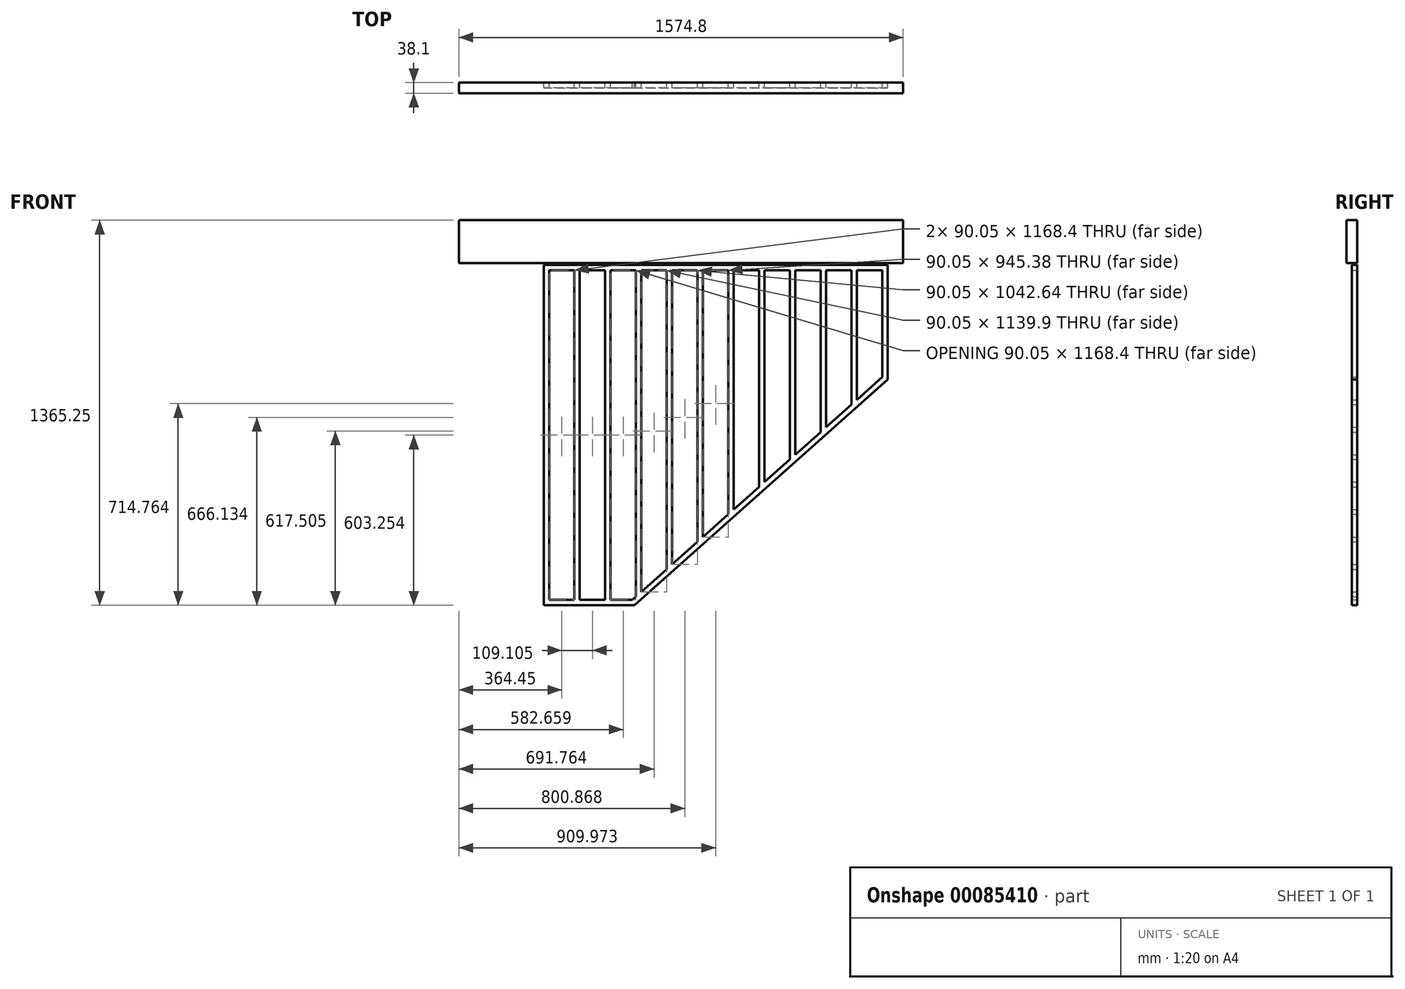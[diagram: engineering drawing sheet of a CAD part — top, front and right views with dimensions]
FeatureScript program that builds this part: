
annotation { "Feature Type Name" : "Feature", "Feature Type Description" : "" }
export const myFeature = defineFeature(function(context is Context, id is Id, definition is map)
    precondition{}
    {
        {
            var Q0;
            Q0=qCreatedBy(makeId("Front.planeOp"),FACE);
            var sketch = newSketch(context, id + "F0", { "sketchPlane" : qUnion([Q0])});
            skLineSegment(sketch, "E0", {"start": v(-309.23, 318.46) * mm, "end": v(-309.23, -888.04) * mm});
            skLineSegment(sketch, "E1", {"start": v(-309.23, -888.04) * mm, "end": v(12.42, -888.04) * mm});
            skLineSegment(sketch, "E2", {"start": v(12.42, -888.04) * mm, "end": v(909.97, -87.94) * mm});
            skLineSegment(sketch, "E3", {"start": v(909.97, -87.94) * mm, "end": v(909.97, 318.46) * mm});
            skLineSegment(sketch, "E4", {"start": v(909.97, 318.46) * mm, "end": v(-309.23, 318.46) * mm});
            skLineSegment(sketch, "E5.0", {"start": v(-290.18, 299.41) * mm, "end": v(-290.18, -868.99) * mm});
            skLineSegment(sketch, "E5.1", {"start": v(890.92, 299.41) * mm, "end": v(800.87, 299.41) * mm});
            skLineSegment(sketch, "E5.2", {"start": v(-290.18, -868.99) * mm, "end": v(-200.12, -868.99) * mm});
            skLineSegment(sketch, "E5.3", {"start": v(5.16, -868.99) * mm, "end": v(18.09, -857.47) * mm});
            skLineSegment(sketch, "E5.4", {"start": v(890.92, -79.4) * mm, "end": v(890.92, 299.41) * mm});
            skLineSegment(sketch, "E6.0", {"start": v(-200.12, 299.41) * mm, "end": v(-200.12, -868.99) * mm});
            skLineSegment(sketch, "E7.0", {"start": v(-181.07, 299.41) * mm, "end": v(-181.07, -868.99) * mm});
            skLineSegment(sketch, "E8.direction1", {"start": v(-181.07, -868.99) * mm, "end": v(-155.67, -868.99) * mm, "construction": true});
            skLineSegment(sketch, "E9", {"start": v(-91.02, 299.41) * mm, "end": v(-91.02, -868.99) * mm});
            skLineSegment(sketch, "E10", {"start": v(-71.97, 299.41) * mm, "end": v(-71.97, -868.99) * mm});
            skLineSegment(sketch, "E11.0", {"start": v(18.09, 299.41) * mm, "end": v(18.09, -857.47) * mm});
            skLineSegment(sketch, "E12.0", {"start": v(37.14, 299.41) * mm, "end": v(37.14, -840.48) * mm});
            skLineSegment(sketch, "E13.0", {"start": v(127.2, 299.41) * mm, "end": v(127.2, -760.2) * mm});
            skLineSegment(sketch, "E14.0", {"start": v(146.24, 299.41) * mm, "end": v(146.24, -743.23) * mm});
            skLineSegment(sketch, "E15.0", {"start": v(236.3, 299.41) * mm, "end": v(236.3, -662.95) * mm});
            skLineSegment(sketch, "E16.0", {"start": v(255.35, 299.41) * mm, "end": v(255.35, -645.97) * mm});
            skLineSegment(sketch, "E17.0", {"start": v(345.4, 299.41) * mm, "end": v(345.4, -565.7) * mm});
            skLineSegment(sketch, "E18.0", {"start": v(364.45, 299.41) * mm, "end": v(364.45, -548.7) * mm});
            skLineSegment(sketch, "E19.0", {"start": v(454.5, 299.41) * mm, "end": v(454.5, -468.43) * mm});
            skLineSegment(sketch, "E20.0", {"start": v(473.55, 299.41) * mm, "end": v(473.55, -451.45) * mm});
            skLineSegment(sketch, "E21.0", {"start": v(563.6, 299.41) * mm, "end": v(563.6, -371.17) * mm});
            skLineSegment(sketch, "E22.0", {"start": v(582.66, 299.41) * mm, "end": v(582.66, -354.2) * mm});
            skLineSegment(sketch, "E23.0", {"start": v(672.71, 299.41) * mm, "end": v(672.71, -273.91) * mm});
            skLineSegment(sketch, "E24.0", {"start": v(691.76, 299.41) * mm, "end": v(691.76, -256.93) * mm});
            skLineSegment(sketch, "E25.0", {"start": v(781.82, 299.41) * mm, "end": v(781.82, -176.66) * mm});
            skLineSegment(sketch, "E26.0", {"start": v(800.87, 299.41) * mm, "end": v(800.87, -159.67) * mm});
            skLineSegment(sketch, "E27.trimOffspring", {"start": v(-200.12, 299.41) * mm, "end": v(-290.18, 299.41) * mm});
            skLineSegment(sketch, "E28.trimOffspring", {"start": v(-91.02, 299.41) * mm, "end": v(-181.07, 299.41) * mm});
            skLineSegment(sketch, "E29.trimOffspring", {"start": v(18.09, 299.41) * mm, "end": v(-71.97, 299.41) * mm});
            skLineSegment(sketch, "E30.trimOffspring", {"start": v(127.2, 299.41) * mm, "end": v(37.14, 299.41) * mm});
            skLineSegment(sketch, "E31.trimOffspring", {"start": v(236.3, 299.41) * mm, "end": v(146.24, 299.41) * mm});
            skLineSegment(sketch, "E32.trimOffspring", {"start": v(454.5, 299.41) * mm, "end": v(364.45, 299.41) * mm});
            skLineSegment(sketch, "E33.trimOffspring", {"start": v(345.4, 299.41) * mm, "end": v(255.35, 299.41) * mm});
            skLineSegment(sketch, "E34.trimOffspring", {"start": v(563.6, 299.41) * mm, "end": v(473.55, 299.41) * mm});
            skLineSegment(sketch, "E35.trimOffspring", {"start": v(672.71, 299.41) * mm, "end": v(582.66, 299.41) * mm});
            skLineSegment(sketch, "E36.trimOffspring", {"start": v(781.82, 299.41) * mm, "end": v(691.76, 299.41) * mm});
            skLineSegment(sketch, "E37.trimOffspring", {"start": v(-181.07, -868.99) * mm, "end": v(-91.02, -868.99) * mm});
            skLineSegment(sketch, "E38.trimOffspring", {"start": v(-71.97, -868.99) * mm, "end": v(5.16, -868.99) * mm});
            skLineSegment(sketch, "E39.trimOffspring", {"start": v(37.14, -840.48) * mm, "end": v(127.2, -760.2) * mm});
            skLineSegment(sketch, "E40.trimOffspring", {"start": v(146.24, -743.23) * mm, "end": v(236.3, -662.95) * mm});
            skLineSegment(sketch, "E41.trimOffspring", {"start": v(255.35, -645.97) * mm, "end": v(345.4, -565.7) * mm});
            skLineSegment(sketch, "E42.trimOffspring", {"start": v(364.45, -548.7) * mm, "end": v(454.5, -468.43) * mm});
            skLineSegment(sketch, "E43.trimOffspring", {"start": v(473.55, -451.45) * mm, "end": v(563.6, -371.17) * mm});
            skLineSegment(sketch, "E44.trimOffspring", {"start": v(582.66, -354.2) * mm, "end": v(672.71, -273.91) * mm});
            skLineSegment(sketch, "E45.trimOffspring", {"start": v(691.76, -256.93) * mm, "end": v(781.82, -176.66) * mm});
            skLineSegment(sketch, "E46.trimOffspring", {"start": v(800.87, -159.67) * mm, "end": v(890.92, -79.4) * mm});
            skLineSegment(sketch, "E47", {"start": v(5.16, -868.99) * mm, "end": v(12.42, -888.04) * mm});
            skLineSegment(sketch, "E48", {"start": v(890.92, -79.4) * mm, "end": v(909.97, -87.94) * mm});
            skSolve(sketch);
        }
        {
            var Q0;
            Q0=makeQuery(id+"F0.imprint","IMPRINT",FACE,{"disambiguationData":[TD([[makeQuery(id+"F0.imprint","IMPRINT",EDGE,{"derivedFrom":sQuery(id+"F0.wireOp",EDGE,"E0")}),1.0]])]});
            extrude(context, id + "F1", {"entities" : qUnion([Q0]), "endBound" : BoundingType.SYMMETRIC, "depth" : 19.05 * mm});
        }
        {
            var Q0;
            Q0=qCreatedBy(makeId("Right.planeOp"),FACE);
            var sketch = newSketch(context, id + "F2", { "sketchPlane" : qUnion([Q0])});
            skLineSegment(sketch, "E49.bottom", {"start": v(9.52, 477.21) * mm, "end": v(-28.58, 477.21) * mm});
            skLineSegment(sketch, "E49.top", {"start": v(9.52, 324.81) * mm, "end": v(-28.57, 324.81) * mm});
            skLineSegment(sketch, "E49.left", {"start": v(9.52, 477.21) * mm, "end": v(9.53, 324.81) * mm});
            skLineSegment(sketch, "E49.right", {"start": v(-28.58, 477.21) * mm, "end": v(-28.57, 324.81) * mm});
            skLineSegment(sketch, "E50", {"start": v(9.53, 324.81) * mm, "end": v(9.53, 318.46) * mm, "construction": true});
            skSolve(sketch);
        }
        {
            var Q0;
            Q0=makeQuery(id+"F2.imprint","IMPRINT",FACE,{"disambiguationData":[TD([[makeQuery(id+"F2.imprint","IMPRINT",EDGE,{"derivedFrom":sQuery(id+"F2.wireOp",EDGE,"E49.bottom")}),1.0]])]});
            extrude(context, id + "F3", {"entities" : qUnion([Q0]), "depth" : 965.2 * mm, "hasSecondDirection" : true, "secondDirectionOppositeDirection" : true, "secondDirectionDepth" : 609.6 * mm});
        }
    });
